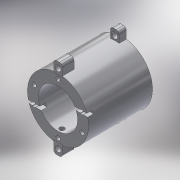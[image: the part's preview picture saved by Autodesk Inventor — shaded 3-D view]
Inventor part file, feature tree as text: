
AUTODESK INVENTOR PART (.ipt)
format: ipt  version: 2018.2 (Build 222227000, 227)  size: 279,552 bytes
history: native  units: in
note: dims shown in document units (in); Inventor stores cm internally (conversion verified against a paired STEP export)
features: sketch x4, extrude x3, mirror x2, direct_edit x1, pattern_circular x1, revolve x1, move_body x1
ambient origin geometry x8: Origin, YZ Plane, XZ Plane, XY Plane, X Axis, Y Axis, Z Axis, Center Point
bodies: Solid1 (feature_tree)
feature tree (13):
  direct_edit  "Direct Edit1"
  extrude  "Extrusion1"  Depth=0.0787in
  extrude  "Extrusion2"  Depth=0.1575in TaperAngle=0.0deg
  pattern_circular  "Circular Pattern1"  [2 undecoded]
  extrude  "Extrusion3"  Depth=0.7874in TaperAngle=360.0deg
  mirror  "Mirror1"
  revolve  "Revolution1"  [1 undecoded]
  sketch  "Sketch2"  dims[d0=0.0in d1=0.0in d2=0.1181in d3=0.0787in]
  sketch  "Sketch3"  dims[d4=0.1969in d5=0.1575in d6=0.0in]
  sketch  "Sketch4"  dims[d7=0.1339in]
  sketch  "Sketch5"  dims[d8=0.0492in d9=0.6299in d10=0.6299in d11=0.0in d12=0.0in d13=0.7874in d14=360.0deg d16=0.1181in d17=0.1181in d18=1.378in d19=0.2362in d20=0.1181in d21=0.3937in d22=0.0in d23=90.0deg]
  mirror  "Mirror7"
  move_body  "Move1"
note: 3 required parameter values undecoded (feature->parameter linkage not recoverable at this tier; creation-order binding heuristic only, values carry confidence <= 0.55)